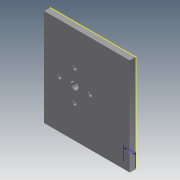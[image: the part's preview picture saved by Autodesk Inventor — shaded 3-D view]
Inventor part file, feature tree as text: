
AUTODESK INVENTOR PART (.ipt)
format: ipt  version: 2011 (Build 150239000, 239)  size: 116,224 bytes
history: native  units: in
note: dims shown in document units (in); Inventor stores cm internally (conversion verified against a paired STEP export)
features: extrude x5, sketch x5
ambient origin geometry x8: Origin, YZ Plane, XZ Plane, XY Plane, X Axis, Y Axis, Z Axis, Center Point
bodies: Solid1 (feature_tree)
feature tree (10):
  extrude  "Extrusion1"  Depth=2.0079in
  extrude  "Extrusion2"  Depth=0.9843in
  extrude  "Extrusion3"  Depth=0.0787in
  extrude  "Extrusion4"  Depth=0.0787in
  extrude  "Extrusion5"  Depth=0.6299in
  sketch  "Sketch1"  dims[d0=1.7717in d1=2.0079in]
  sketch  "Sketch2"  dims[d2=0.125in d3=0.0in d4=0.9843in]
  sketch  "Sketch3"  dims[d6=0.6299in d7=0.0787in]
  sketch  "Sketch4"  dims[d8=0.0787in d9=0.0787in]
  sketch  "Sketch5"  dims[d10=0.0787in d11=0.6299in d12=1.0in d13=0.0in d14=0.156in d15=1.0in d16=0.0in d17=0.25in d18=0.125in d19=0.0in d20=0.125in d21=0.0in]
